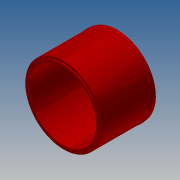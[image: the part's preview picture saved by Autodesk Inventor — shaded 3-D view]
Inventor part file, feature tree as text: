
AUTODESK INVENTOR PART (.ipt)
format: ipt  version: 2017.3 (Build 213257000, 257)  size: 147,456 bytes
history: native  units: in
note: dims shown in document units (in); Inventor stores cm internally (conversion verified against a paired STEP export)
features: extrude x4, sketch x4, chamfer x2, fillet x1
ambient origin geometry x8: Origin, YZ Plane, XZ Plane, XY Plane, X Axis, Y Axis, Z Axis, Center Point
bodies: Solid1 (feature_tree)
feature tree (11):
  extrude  "Extrusion1"  Depth=32.5in
  extrude  "Extrusion2"  Depth=22.7165in
  extrude  "Extrusion3"  Depth=1.0in
  chamfer  "Chamfer1"  Distance=1.0in
  extrude  "Extrusion4"  Depth=0.0312in TaperAngle=45.0deg
  fillet  "Fillet1"  Radius=30.48in
  chamfer  "Chamfer2"  Distance=0.5in
  sketch  "Sketch1"  dims[d0=28.5in d1=32.5in]
  sketch  "Sketch2"  dims[d2=22.7165in d3=0.0in d4=32.75in]
  sketch  "Sketch3"  dims[d5=2.0in d6=0.0in d7=32.48in d8=1.0in d9=0.0in]
  sketch  "Sketch4"  dims[d10=0.125in d11=0.125in d12=45.0deg d13=30.48in d14=0.5in d15=0.0in d16=0.0312in d17=0.0312in d18=0.125in d19=45.0deg]
